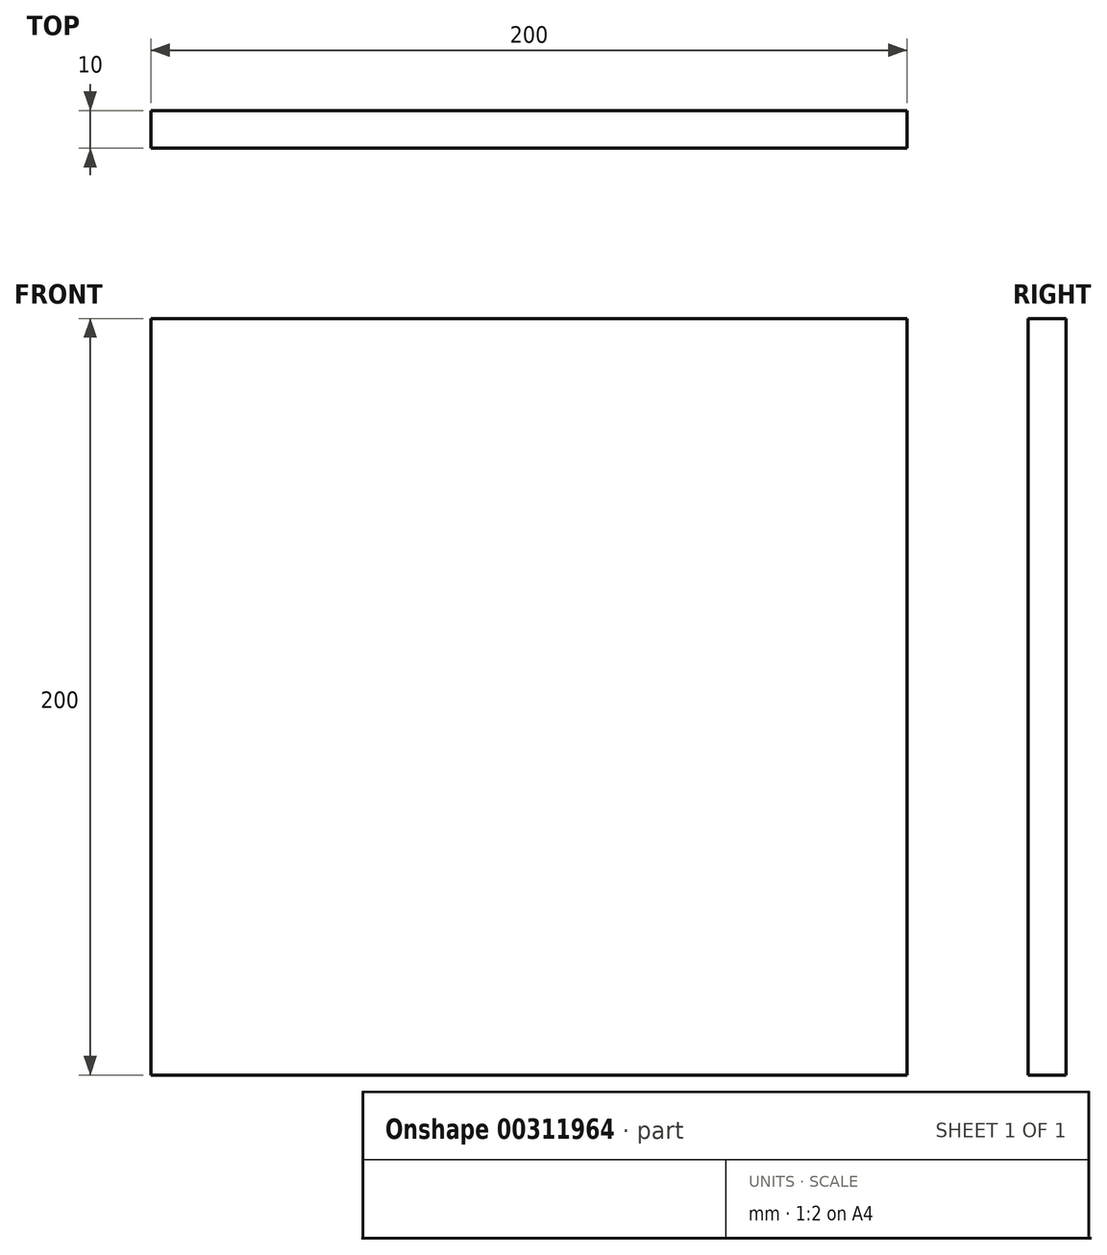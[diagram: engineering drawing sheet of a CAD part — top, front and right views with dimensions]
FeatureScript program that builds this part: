
annotation { "Feature Type Name" : "Feature", "Feature Type Description" : "" }
export const myFeature = defineFeature(function(context is Context, id is Id, definition is map)
    precondition{}
    {
        {
            var Q0;
            Q0=qCreatedBy(makeId("Front.planeOp"),FACE);
            var sketch = newSketch(context, id + "F0", { "sketchPlane" : qUnion([Q0])});
            skLineSegment(sketch, "E0.bottom", {"start": v(-100, 100) * mm, "end": v(100, 100) * mm});
            skLineSegment(sketch, "E0.top", {"start": v(-100, -100) * mm, "end": v(100, -100) * mm});
            skLineSegment(sketch, "E0.left", {"start": v(-100, 100) * mm, "end": v(-100, -100) * mm});
            skLineSegment(sketch, "E0.right", {"start": v(100, 100) * mm, "end": v(100, -100) * mm});
            skPoint(sketch, "E0.middle", {"position": v(0, 0) * mm});
            skSolve(sketch);
        }
        {
            var Q0;
            Q0 = qSketchRegion(id + "F0", true);
            extrude(context, id + "F1", {"entities" : qUnion([Q0]), "depth" : 10 * mm});
        }
    });
